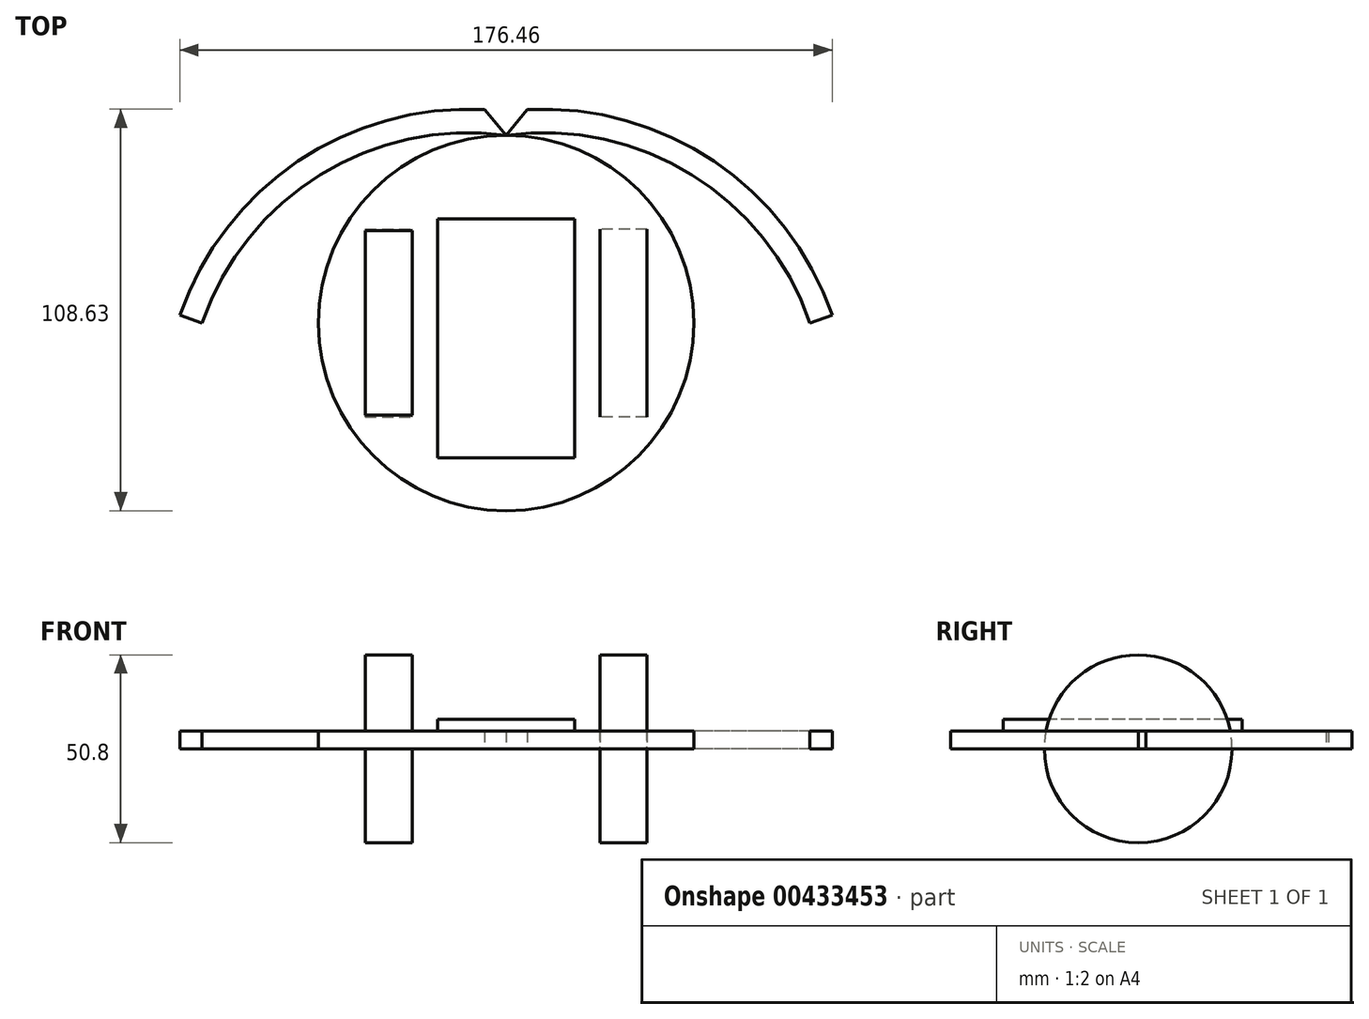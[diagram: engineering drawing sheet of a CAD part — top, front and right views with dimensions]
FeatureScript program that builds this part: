
annotation { "Feature Type Name" : "Feature", "Feature Type Description" : "" }
export const myFeature = defineFeature(function(context is Context, id is Id, definition is map)
    precondition{}
    {
        {
            var Q0;
            Q0=qCreatedBy(makeId("Top.planeOp"),FACE);
            var sketch = newSketch(context, id + "F0", { "sketchPlane" : qUnion([Q0])});
            skCircle(sketch, "E0", {"center": v(0, 0) * mm, "radius": 50.8 * mm});
            skArc(sketch, "E1", {"start": v(0, 50.8) * mm, "mid": v(-50.2, 40.1) * mm, "end": v(-82.24, 0) * mm});
            skArc(sketch, "E2", {"start": v(82.24, 0) * mm, "mid": v(50.2, 40.1) * mm, "end": v(0, 50.8) * mm});
            skArc(sketch, "E3.0", {"start": v(-5.78, 57.71) * mm, "mid": v(-56.32, 43.72) * mm, "end": v(-88.23, 2.1) * mm});
            skArc(sketch, "E4.0", {"start": v(88.23, 2.1) * mm, "mid": v(56.33, 43.71) * mm, "end": v(5.8, 57.72) * mm});
            skLineSegment(sketch, "E5", {"start": v(82.24, 0) * mm, "end": v(88.23, 2.1) * mm});
            skLineSegment(sketch, "E6", {"start": v(-88.23, 2.1) * mm, "end": v(-82.24, 0) * mm});
            skLineSegment(sketch, "E7", {"start": v(-5.78, 57.71) * mm, "end": v(0, 50.8) * mm});
            skLineSegment(sketch, "E8", {"start": v(5.8, 57.72) * mm, "end": v(0, 50.8) * mm});
            skSolve(sketch);
        }
        {
            var Q0;
            Q0 = qSketchRegion(id + "F0", true);
            extrude(context, id + "F1", {"entities" : qUnion([Q0]), "depth" : 4.76 * mm});
        }
        {
            var Q0;
            Q0=qCreatedBy(makeId("Right.planeOp"),FACE);
            cPlane(context, id + "F2", {"entities" : qUnion([Q0]), "cplaneType" : CPlaneType.OFFSET, "offset" : 25.4 * mm, "width" : 152.4 * mm, "height" : 152.4 * mm});
        }
        {
            var Q0;
            Q0=qCreatedBy(id+"F2.planeOp",FACE);
            var sketch = newSketch(context, id + "F3", { "sketchPlane" : qUnion([Q0])});
            skCircle(sketch, "E9", {"center": v(0, 0) * mm, "radius": 25.4 * mm});
            skSolve(sketch);
        }
        {
            var Q0;
            Q0 = qSketchRegion(id + "F3", true);
            extrude(context, id + "F4", {"entities" : qUnion([Q0]), "depth" : 12.7 * mm});
        }
        {
            var Q0;
            Q0=qCreatedBy(makeId("Right.planeOp"),FACE);
            cPlane(context, id + "F5", {"entities" : qUnion([Q0]), "cplaneType" : CPlaneType.OFFSET, "offset" : 25.4 * mm, "oppositeDirection" : true, "width" : 152.4 * mm, "height" : 152.4 * mm});
        }
        {
            var Q0;
            Q0=qCreatedBy(id+"F5.planeOp",FACE);
            var sketch = newSketch(context, id + "F6", { "sketchPlane" : qUnion([Q0])});
            skCircle(sketch, "E10.0", {"center": v(0, 0) * mm, "radius": 25.4 * mm});
            skSolve(sketch);
        }
        {
            var Q0;
            Q0 = qSketchRegion(id + "F6", true);
            extrude(context, id + "F7", {"entities" : qUnion([Q0]), "operationType" : NewBodyOperationType.ADD, "oppositeDirection" : true, "depth" : 12.7 * mm});
        }
        {
            var Q0;
            Q0=makeQuery(id+"F1.opExtrude","CAP_FACE",FACE,{"disambiguationData":[OSD([sQuery(id+"F0.wireOp",EDGE,"E0")])],"isStart":false});
            var sketch = newSketch(context, id + "F8", { "sketchPlane" : qUnion([Q0])});
            skLineSegment(sketch, "E11.bottom", {"start": v(-18.5, 28.15) * mm, "end": v(18.5, 28.15) * mm});
            skLineSegment(sketch, "E11.top", {"start": v(-18.5, -36.46) * mm, "end": v(18.5, -36.46) * mm});
            skLineSegment(sketch, "E11.left", {"start": v(-18.5, 28.15) * mm, "end": v(-18.5, -36.46) * mm});
            skLineSegment(sketch, "E11.right", {"start": v(18.5, 28.15) * mm, "end": v(18.5, -36.46) * mm});
            skPoint(sketch, "E11.middle", {"position": v(0, -4.16) * mm});
            skSolve(sketch);
        }
        {
            var Q0;
            Q0 = qSketchRegion(id + "F8", true);
            extrude(context, id + "F9", {"entities" : qUnion([Q0]), "operationType" : NewBodyOperationType.ADD, "depth" : 3.17 * mm});
        }
    });
